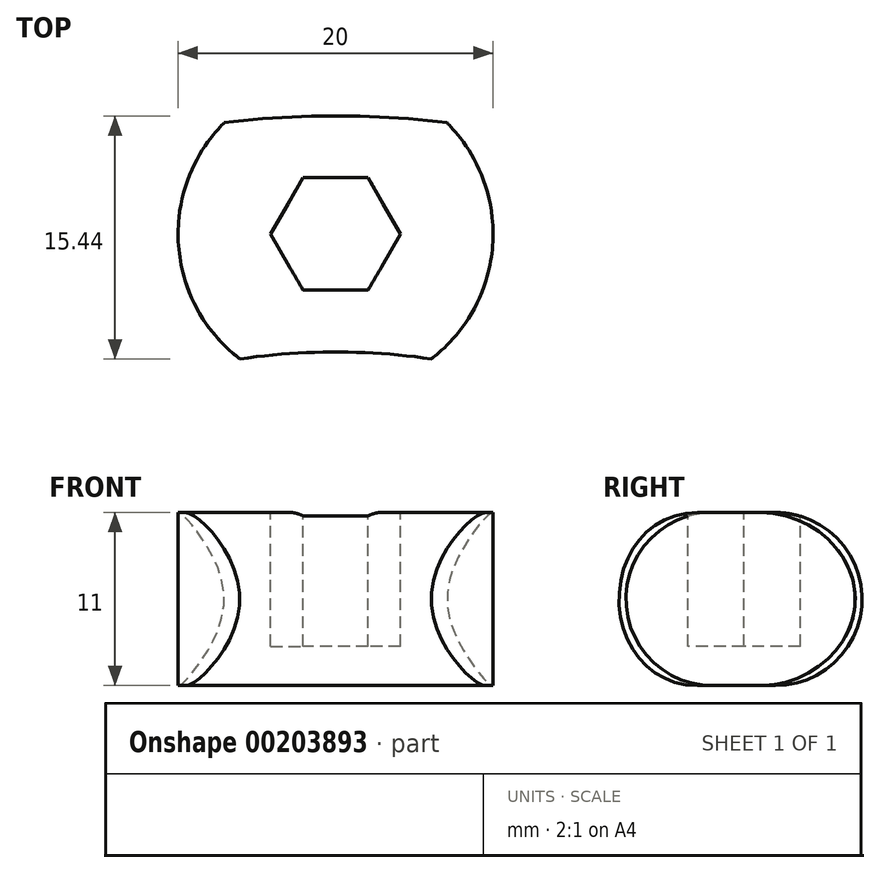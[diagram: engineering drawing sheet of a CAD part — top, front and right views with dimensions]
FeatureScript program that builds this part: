
annotation { "Feature Type Name" : "Feature", "Feature Type Description" : "" }
export const myFeature = defineFeature(function(context is Context, id is Id, definition is map)
    precondition{}
    {
        {
            var Q0;
            Q0=qCreatedBy(makeId("Front.planeOp"),FACE);
            var sketch = newSketch(context, id + "F0", { "sketchPlane" : qUnion([Q0])});
            skLineSegment(sketch, "E0.bottom", {"start": v(42.5, 11) * mm, "end": v(57.5, 11) * mm});
            skLineSegment(sketch, "E0.top", {"start": v(42.5, 0) * mm, "end": v(57.5, 0) * mm});
            skLineSegment(sketch, "E0.left", {"start": v(42.5, 11) * mm, "end": v(42.5, 0) * mm});
            skLineSegment(sketch, "E0.right", {"start": v(57.5, 11) * mm, "end": v(57.5, 0) * mm});
            skLineSegment(sketch, "E1", {"start": v(0, 0) * mm, "end": v(0, 22.77) * mm});
            skSolve(sketch);
        }
        {
            var Q0;
            Q0=qSketchRegion(id+"F0",true);
            var Q1;
            Q1=sQuery(id+"F0.wireOp",EDGE,"E1");
            revolve(context, id + "F1", {"entities" : qUnion([Q0]), "axis" : qUnion([Q1]), "revolveType" : RevolveType.FULL});
        }
        {
            var Q0;
            Q0=makeQuery(id+"F1.opRevolve","SWEPT_FACE",FACE,{"disambiguationData":[OSD([sQuery(id+"F0.wireOp",EDGE,"E0.bottom")])]});
            var sketch = newSketch(context, id + "F2", { "sketchPlane" : qUnion([Q0])});
            skCircle(sketch, "E2.cCircle", {"center": v(0, 50) * mm, "radius": 3.58 * mm, "construction": true});
            skLineSegment(sketch, "E2.0", {"start": v(2.06, 46.43) * mm, "end": v(-2.06, 46.43) * mm});
            skLineSegment(sketch, "E2.1", {"start": v(-2.06, 46.43) * mm, "end": v(-4.13, 50) * mm});
            skLineSegment(sketch, "E2.2", {"start": v(-4.13, 50) * mm, "end": v(-2.06, 53.58) * mm});
            skLineSegment(sketch, "E2.3", {"start": v(-2.06, 53.58) * mm, "end": v(2.06, 53.58) * mm});
            skLineSegment(sketch, "E2.4", {"start": v(2.06, 53.57) * mm, "end": v(4.13, 50) * mm});
            skLineSegment(sketch, "E2.5", {"start": v(4.13, 50) * mm, "end": v(2.06, 46.43) * mm});
            skPoint(sketch, "E2.0.midPoint", {"position": v(0, 46.43) * mm});
            skCircle(sketch, "E3.1.0", {"center": v(-19.13, 46.2) * mm, "radius": 3.58 * mm, "construction": true});
            skPoint(sketch, "E3.1.1", {"position": v(-17.77, 42.9) * mm});
            skLineSegment(sketch, "E3.1.2", {"start": v(-15.32, 47.77) * mm, "end": v(-15.86, 43.68) * mm});
            skLineSegment(sketch, "E3.1.3", {"start": v(-18.6, 50.29) * mm, "end": v(-15.32, 47.77) * mm});
            skLineSegment(sketch, "E3.1.4", {"start": v(-22.4, 48.7) * mm, "end": v(-18.6, 50.29) * mm});
            skLineSegment(sketch, "E3.1.5", {"start": v(-22.95, 44.61) * mm, "end": v(-22.4, 48.7) * mm});
            skLineSegment(sketch, "E3.1.6", {"start": v(-19.67, 42.1) * mm, "end": v(-22.95, 44.61) * mm});
            skLineSegment(sketch, "E3.1.7", {"start": v(-15.86, 43.68) * mm, "end": v(-19.67, 42.1) * mm});
            skCircle(sketch, "E3.2.0", {"center": v(-35.36, 35.36) * mm, "radius": 3.58 * mm, "construction": true});
            skPoint(sketch, "E3.2.1", {"position": v(-32.83, 32.83) * mm});
            skLineSegment(sketch, "E3.2.2", {"start": v(-32.44, 38.27) * mm, "end": v(-31.37, 34.29) * mm});
            skLineSegment(sketch, "E3.2.3", {"start": v(-36.42, 39.34) * mm, "end": v(-32.44, 38.27) * mm});
            skLineSegment(sketch, "E3.2.4", {"start": v(-39.34, 36.42) * mm, "end": v(-36.42, 39.34) * mm});
            skLineSegment(sketch, "E3.2.5", {"start": v(-38.27, 32.44) * mm, "end": v(-39.34, 36.42) * mm});
            skLineSegment(sketch, "E3.2.6", {"start": v(-34.29, 31.37) * mm, "end": v(-38.27, 32.44) * mm});
            skLineSegment(sketch, "E3.2.7", {"start": v(-31.37, 34.29) * mm, "end": v(-34.29, 31.37) * mm});
            skCircle(sketch, "E3.3.0", {"center": v(-46.2, 19.13) * mm, "radius": 3.58 * mm, "construction": true});
            skPoint(sketch, "E3.3.1", {"position": v(-42.9, 17.77) * mm});
            skLineSegment(sketch, "E3.3.2", {"start": v(-44.61, 22.95) * mm, "end": v(-42.1, 19.67) * mm});
            skLineSegment(sketch, "E3.3.3", {"start": v(-48.7, 22.4) * mm, "end": v(-44.61, 22.95) * mm});
            skLineSegment(sketch, "E3.3.4", {"start": v(-50.29, 18.6) * mm, "end": v(-48.7, 22.4) * mm});
            skLineSegment(sketch, "E3.3.5", {"start": v(-47.77, 15.32) * mm, "end": v(-50.29, 18.6) * mm});
            skLineSegment(sketch, "E3.3.6", {"start": v(-43.68, 15.86) * mm, "end": v(-47.77, 15.32) * mm});
            skLineSegment(sketch, "E3.3.7", {"start": v(-42.1, 19.67) * mm, "end": v(-43.68, 15.86) * mm});
            skCircle(sketch, "E3.4.0", {"center": v(-50, 0) * mm, "radius": 3.58 * mm, "construction": true});
            skPoint(sketch, "E3.4.1", {"position": v(-46.42, 0) * mm});
            skLineSegment(sketch, "E3.4.2", {"start": v(-50, 4.13) * mm, "end": v(-46.43, 2.06) * mm});
            skLineSegment(sketch, "E3.4.3", {"start": v(-53.57, 2.06) * mm, "end": v(-50, 4.13) * mm});
            skLineSegment(sketch, "E3.4.4", {"start": v(-53.57, -2.06) * mm, "end": v(-53.57, 2.06) * mm});
            skLineSegment(sketch, "E3.4.5", {"start": v(-50, -4.13) * mm, "end": v(-53.58, -2.06) * mm});
            skLineSegment(sketch, "E3.4.6", {"start": v(-46.43, -2.06) * mm, "end": v(-50, -4.13) * mm});
            skLineSegment(sketch, "E3.4.7", {"start": v(-46.42, 2.06) * mm, "end": v(-46.42, -2.06) * mm});
            skCircle(sketch, "E3.5.0", {"center": v(-46.2, -19.13) * mm, "radius": 3.58 * mm, "construction": true});
            skPoint(sketch, "E3.5.1", {"position": v(-42.9, -17.77) * mm});
            skLineSegment(sketch, "E3.5.2", {"start": v(-47.77, -15.32) * mm, "end": v(-43.68, -15.86) * mm});
            skLineSegment(sketch, "E3.5.3", {"start": v(-50.29, -18.6) * mm, "end": v(-47.77, -15.32) * mm});
            skLineSegment(sketch, "E3.5.4", {"start": v(-48.7, -22.4) * mm, "end": v(-50.29, -18.6) * mm});
            skLineSegment(sketch, "E3.5.5", {"start": v(-44.61, -22.95) * mm, "end": v(-48.7, -22.4) * mm});
            skLineSegment(sketch, "E3.5.6", {"start": v(-42.1, -19.67) * mm, "end": v(-44.61, -22.95) * mm});
            skLineSegment(sketch, "E3.5.7", {"start": v(-43.68, -15.86) * mm, "end": v(-42.1, -19.67) * mm});
            skCircle(sketch, "E3.6.0", {"center": v(-35.36, -35.36) * mm, "radius": 3.58 * mm, "construction": true});
            skPoint(sketch, "E3.6.1", {"position": v(-32.83, -32.83) * mm});
            skLineSegment(sketch, "E3.6.2", {"start": v(-38.27, -32.44) * mm, "end": v(-34.29, -31.37) * mm});
            skLineSegment(sketch, "E3.6.3", {"start": v(-39.34, -36.42) * mm, "end": v(-38.27, -32.44) * mm});
            skLineSegment(sketch, "E3.6.4", {"start": v(-36.42, -39.34) * mm, "end": v(-39.34, -36.42) * mm});
            skLineSegment(sketch, "E3.6.5", {"start": v(-32.44, -38.27) * mm, "end": v(-36.42, -39.34) * mm});
            skLineSegment(sketch, "E3.6.6", {"start": v(-31.37, -34.29) * mm, "end": v(-32.44, -38.27) * mm});
            skLineSegment(sketch, "E3.6.7", {"start": v(-34.29, -31.37) * mm, "end": v(-31.37, -34.29) * mm});
            skCircle(sketch, "E3.7.0", {"center": v(-19.13, -46.2) * mm, "radius": 3.58 * mm, "construction": true});
            skPoint(sketch, "E3.7.1", {"position": v(-17.77, -42.9) * mm});
            skLineSegment(sketch, "E3.7.2", {"start": v(-22.95, -44.61) * mm, "end": v(-19.67, -42.1) * mm});
            skLineSegment(sketch, "E3.7.3", {"start": v(-22.4, -48.7) * mm, "end": v(-22.95, -44.61) * mm});
            skLineSegment(sketch, "E3.7.4", {"start": v(-18.6, -50.29) * mm, "end": v(-22.4, -48.7) * mm});
            skLineSegment(sketch, "E3.7.5", {"start": v(-15.32, -47.77) * mm, "end": v(-18.6, -50.29) * mm});
            skLineSegment(sketch, "E3.7.6", {"start": v(-15.86, -43.68) * mm, "end": v(-15.32, -47.77) * mm});
            skLineSegment(sketch, "E3.7.7", {"start": v(-19.67, -42.1) * mm, "end": v(-15.86, -43.68) * mm});
            skCircle(sketch, "E3.8.0", {"center": v(0, -50) * mm, "radius": 3.58 * mm, "construction": true});
            skPoint(sketch, "E3.8.1", {"position": v(0, -46.43) * mm});
            skLineSegment(sketch, "E3.8.2", {"start": v(-4.13, -50) * mm, "end": v(-2.06, -46.43) * mm});
            skLineSegment(sketch, "E3.8.3", {"start": v(-2.06, -53.57) * mm, "end": v(-4.13, -50) * mm});
            skLineSegment(sketch, "E3.8.4", {"start": v(2.06, -53.58) * mm, "end": v(-2.06, -53.58) * mm});
            skLineSegment(sketch, "E3.8.5", {"start": v(4.13, -50) * mm, "end": v(2.06, -53.58) * mm});
            skLineSegment(sketch, "E3.8.6", {"start": v(2.06, -46.43) * mm, "end": v(4.13, -50) * mm});
            skLineSegment(sketch, "E3.8.7", {"start": v(-2.06, -46.43) * mm, "end": v(2.06, -46.43) * mm});
            skCircle(sketch, "E3.9.0", {"center": v(19.13, -46.2) * mm, "radius": 3.58 * mm, "construction": true});
            skPoint(sketch, "E3.9.1", {"position": v(17.77, -42.9) * mm});
            skLineSegment(sketch, "E3.9.2", {"start": v(15.32, -47.77) * mm, "end": v(15.86, -43.68) * mm});
            skLineSegment(sketch, "E3.9.3", {"start": v(18.6, -50.29) * mm, "end": v(15.32, -47.77) * mm});
            skLineSegment(sketch, "E3.9.4", {"start": v(22.4, -48.7) * mm, "end": v(18.6, -50.29) * mm});
            skLineSegment(sketch, "E3.9.5", {"start": v(22.95, -44.61) * mm, "end": v(22.4, -48.7) * mm});
            skLineSegment(sketch, "E3.9.6", {"start": v(19.67, -42.1) * mm, "end": v(22.95, -44.61) * mm});
            skLineSegment(sketch, "E3.9.7", {"start": v(15.86, -43.68) * mm, "end": v(19.67, -42.1) * mm});
            skCircle(sketch, "E3.10.0", {"center": v(35.36, -35.36) * mm, "radius": 3.58 * mm, "construction": true});
            skPoint(sketch, "E3.10.1", {"position": v(32.83, -32.83) * mm});
            skLineSegment(sketch, "E3.10.2", {"start": v(32.44, -38.27) * mm, "end": v(31.37, -34.29) * mm});
            skLineSegment(sketch, "E3.10.3", {"start": v(36.42, -39.34) * mm, "end": v(32.44, -38.27) * mm});
            skLineSegment(sketch, "E3.10.4", {"start": v(39.34, -36.42) * mm, "end": v(36.42, -39.34) * mm});
            skLineSegment(sketch, "E3.10.5", {"start": v(38.27, -32.44) * mm, "end": v(39.34, -36.42) * mm});
            skLineSegment(sketch, "E3.10.6", {"start": v(34.29, -31.37) * mm, "end": v(38.27, -32.44) * mm});
            skLineSegment(sketch, "E3.10.7", {"start": v(31.37, -34.29) * mm, "end": v(34.29, -31.37) * mm});
            skCircle(sketch, "E3.11.0", {"center": v(46.2, -19.13) * mm, "radius": 3.58 * mm, "construction": true});
            skPoint(sketch, "E3.11.1", {"position": v(42.9, -17.77) * mm});
            skLineSegment(sketch, "E3.11.2", {"start": v(44.61, -22.95) * mm, "end": v(42.1, -19.67) * mm});
            skLineSegment(sketch, "E3.11.3", {"start": v(48.7, -22.4) * mm, "end": v(44.61, -22.95) * mm});
            skLineSegment(sketch, "E3.11.4", {"start": v(50.29, -18.6) * mm, "end": v(48.7, -22.4) * mm});
            skLineSegment(sketch, "E3.11.5", {"start": v(47.77, -15.32) * mm, "end": v(50.29, -18.6) * mm});
            skLineSegment(sketch, "E3.11.6", {"start": v(43.68, -15.86) * mm, "end": v(47.77, -15.32) * mm});
            skLineSegment(sketch, "E3.11.7", {"start": v(42.1, -19.67) * mm, "end": v(43.68, -15.86) * mm});
            skPoint(sketch, "E3.center", {"position": v(0, 0) * mm});
            skPoint(sketch, "E4.2.12.0", {"position": v(46.43, 0) * mm});
            skLineSegment(sketch, "E4.3.12.0", {"start": v(50, -4.13) * mm, "end": v(46.43, -2.06) * mm});
            skLineSegment(sketch, "E4.6.12.0", {"start": v(53.57, -2.06) * mm, "end": v(50, -4.13) * mm});
            skLineSegment(sketch, "E4.9.12.0", {"start": v(53.58, 2.06) * mm, "end": v(53.58, -2.06) * mm});
            skLineSegment(sketch, "E4.12.12.0", {"start": v(50, 4.13) * mm, "end": v(53.58, 2.06) * mm});
            skLineSegment(sketch, "E4.15.12.0", {"start": v(46.43, 2.06) * mm, "end": v(50, 4.13) * mm});
            skCircle(sketch, "E4.16.12.0", {"center": v(50, 0) * mm, "radius": 3.58 * mm, "construction": true});
            skLineSegment(sketch, "E4.18.12.0", {"start": v(46.43, -2.06) * mm, "end": v(46.43, 2.06) * mm});
            skPoint(sketch, "E4.2.13.0", {"position": v(42.9, 17.77) * mm});
            skLineSegment(sketch, "E4.3.13.0", {"start": v(47.77, 15.32) * mm, "end": v(43.68, 15.86) * mm});
            skLineSegment(sketch, "E4.6.13.0", {"start": v(50.29, 18.6) * mm, "end": v(47.77, 15.32) * mm});
            skLineSegment(sketch, "E4.9.13.0", {"start": v(48.7, 22.4) * mm, "end": v(50.29, 18.6) * mm});
            skLineSegment(sketch, "E4.12.13.0", {"start": v(44.61, 22.95) * mm, "end": v(48.7, 22.4) * mm});
            skLineSegment(sketch, "E4.15.13.0", {"start": v(42.1, 19.67) * mm, "end": v(44.61, 22.95) * mm});
            skCircle(sketch, "E4.16.13.0", {"center": v(46.2, 19.13) * mm, "radius": 3.58 * mm, "construction": true});
            skLineSegment(sketch, "E4.18.13.0", {"start": v(43.68, 15.86) * mm, "end": v(42.1, 19.67) * mm});
            skPoint(sketch, "E4.2.14.0", {"position": v(32.83, 32.83) * mm});
            skLineSegment(sketch, "E4.3.14.0", {"start": v(38.27, 32.44) * mm, "end": v(34.29, 31.37) * mm});
            skLineSegment(sketch, "E4.6.14.0", {"start": v(39.34, 36.42) * mm, "end": v(38.27, 32.44) * mm});
            skLineSegment(sketch, "E4.9.14.0", {"start": v(36.42, 39.34) * mm, "end": v(39.34, 36.42) * mm});
            skLineSegment(sketch, "E4.12.14.0", {"start": v(32.44, 38.27) * mm, "end": v(36.42, 39.34) * mm});
            skLineSegment(sketch, "E4.15.14.0", {"start": v(31.37, 34.29) * mm, "end": v(32.44, 38.27) * mm});
            skCircle(sketch, "E4.16.14.0", {"center": v(35.36, 35.36) * mm, "radius": 3.58 * mm, "construction": true});
            skLineSegment(sketch, "E4.18.14.0", {"start": v(34.29, 31.37) * mm, "end": v(31.37, 34.29) * mm});
            skPoint(sketch, "E4.2.15.0", {"position": v(17.77, 42.9) * mm});
            skLineSegment(sketch, "E4.3.15.0", {"start": v(22.95, 44.61) * mm, "end": v(19.67, 42.1) * mm});
            skLineSegment(sketch, "E4.6.15.0", {"start": v(22.4, 48.7) * mm, "end": v(22.95, 44.61) * mm});
            skLineSegment(sketch, "E4.9.15.0", {"start": v(18.6, 50.29) * mm, "end": v(22.4, 48.7) * mm});
            skLineSegment(sketch, "E4.12.15.0", {"start": v(15.32, 47.77) * mm, "end": v(18.6, 50.29) * mm});
            skLineSegment(sketch, "E4.15.15.0", {"start": v(15.86, 43.68) * mm, "end": v(15.32, 47.77) * mm});
            skCircle(sketch, "E4.16.15.0", {"center": v(19.13, 46.2) * mm, "radius": 3.58 * mm, "construction": true});
            skLineSegment(sketch, "E4.18.15.0", {"start": v(19.67, 42.1) * mm, "end": v(15.86, 43.68) * mm});
            skSolve(sketch);
        }
        {
            var Q0;
            Q0=qSketchRegion(id+"F2",true);
            extrude(context, id + "F3", {"entities" : qUnion([Q0]), "operationType" : NewBodyOperationType.REMOVE, "oppositeDirection" : true, "depth" : 8.5 * mm});
        }
        {
            var Q0;
            Q0=makeQuery(id+"F1.opRevolve","SWEPT_EDGE",EDGE,{"disambiguationData":[OSD([sQuery(id+"F0.wireOp",EDGE,"E0.bottom"),sQuery(id+"F0.wireOp",EDGE,"E0.left")])]});
            var Q1;
            Q1=makeQuery(id+"F1.opRevolve","SWEPT_EDGE",EDGE,{"disambiguationData":[OSD([sQuery(id+"F0.wireOp",EDGE,"E0.bottom"),sQuery(id+"F0.wireOp",EDGE,"E0.right")])]});
            var Q2;
            Q2=makeQuery(id+"F1.opRevolve","SWEPT_EDGE",EDGE,{"disambiguationData":[OSD([sQuery(id+"F0.wireOp",EDGE,"E0.top"),sQuery(id+"F0.wireOp",EDGE,"E0.right")])]});
            var Q3;
            Q3=makeQuery(id+"F1.opRevolve","SWEPT_EDGE",EDGE,{"disambiguationData":[OSD([sQuery(id+"F0.wireOp",EDGE,"E0.top"),sQuery(id+"F0.wireOp",EDGE,"E0.left")])]});
            fillet(context, id + "F4", {"entities" : qUnion([Q0, Q1, Q2, Q3]), "radius" : 5.5 * mm, "tangentPropagation" : true, "allowEdgeOverflow" : false});
        }
        {
            var Q0;
            Q0=qCreatedBy(makeId("Top.planeOp"),FACE);
            var sketch = newSketch(context, id + "F5", { "sketchPlane" : qUnion([Q0])});
            skCircle(sketch, "E5", {"center": v(0, 50) * mm, "radius": 10 * mm});
            skSolve(sketch);
        }
        {
            var Q0;
            Q0 = qSketchRegion(id + "F5", true);
            extrude(context, id + "F6", {"entities" : qUnion([Q0]), "depth" : 25 * mm});
        }
        {
            var Q0;
            Q0=makeQuery(id+"F6.opExtrude","SWEPT_BODY",BODY,{"disambiguationData":[OSD([sQuery(id+"F5.wireOp",EDGE,"E5")])]});
            var Q1;
            Q1=makeQuery(id+"F1.opRevolve","SWEPT_BODY",BODY,{"disambiguationData":[OSD([sQuery(id+"F0.wireOp",EDGE,"E0.bottom"),sQuery(id+"F0.wireOp",EDGE,"E0.top"),sQuery(id+"F0.wireOp",EDGE,"E0.left"),sQuery(id+"F0.wireOp",EDGE,"E0.right")])]});
            booleanBodies(context, id + "F7", {"operationType" : BooleanOperationType.INTERSECTION, "tools" : qUnion([Q0, Q1])});
        }
    });
